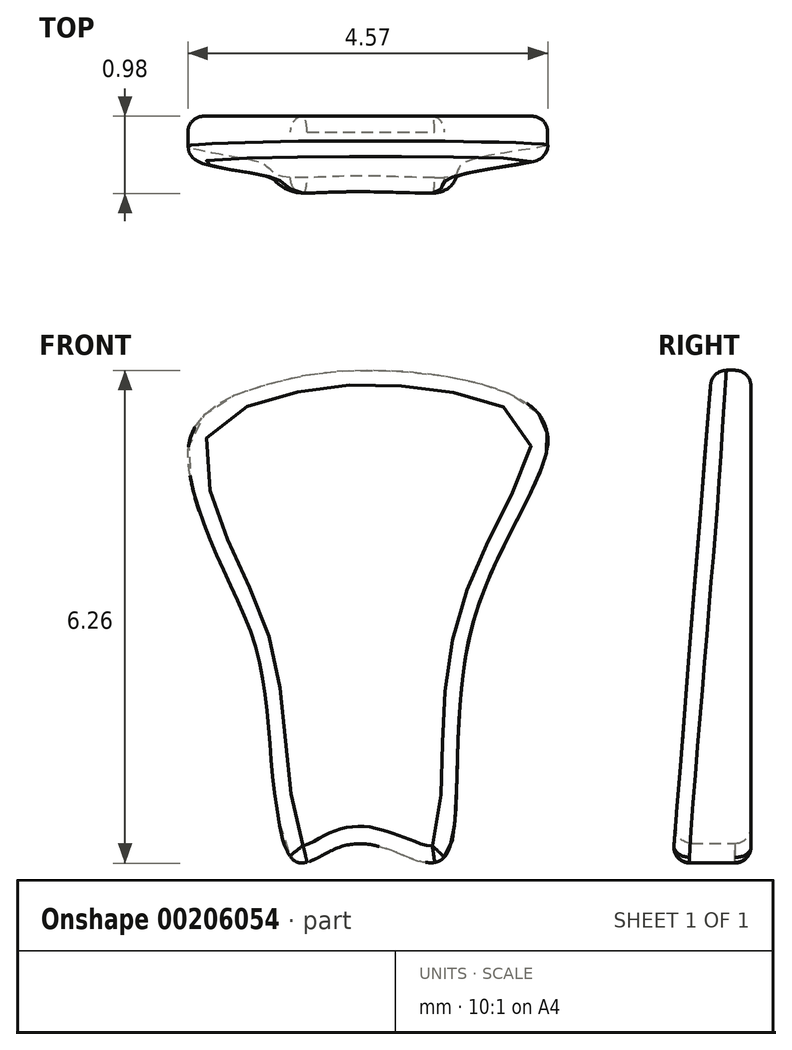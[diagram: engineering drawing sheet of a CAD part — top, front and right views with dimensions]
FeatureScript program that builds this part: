
annotation { "Feature Type Name" : "Feature", "Feature Type Description" : "" }
export const myFeature = defineFeature(function(context is Context, id is Id, definition is map)
    precondition{}
    {
        {
            var Q0;
            Q0=qCreatedBy(makeId("Front.planeOp"),FACE);
            var sketch = newSketch(context, id + "F0", { "sketchPlane" : qUnion([Q0])});
            skPoint(sketch, "E0", {"position": v(-0.76, -3.9) * mm});
            skPoint(sketch, "E1", {"position": v(1.07, -3.89) * mm});
            skPoint(sketch, "E2", {"position": v(1.47, -0.96) * mm});
            skPoint(sketch, "E3", {"position": v(2.4, 1.67) * mm});
            skPoint(sketch, "E4", {"position": v(0.49, 2.33) * mm});
            skPoint(sketch, "E5", {"position": v(-1.15, 2.16) * mm});
            skPoint(sketch, "E6", {"position": v(-2.1, 1.49) * mm});
            skPoint(sketch, "E7", {"position": v(-1.57, -0.44) * mm});
            skPoint(sketch, "E8", {"position": v(-1.15, -1.8) * mm});
            skPoint(sketch, "E9", {"position": v(0, -3.67) * mm});
            skFitSpline(sketch, "E10", {"points": [v(-2.1, 1.49) * mm, v(-1.15, 2.16) * mm, v(0.49, 2.33) * mm, v(2.4, 1.67) * mm, v(1.47, -0.96) * mm, v(1.07, -3.89) * mm, v(0, -3.67) * mm, v(-0.76, -3.9) * mm, v(-1.15, -1.8) * mm, v(-1.57, -0.44) * mm, v(-2.1, 1.49) * mm]});
            skSolve(sketch);
        }
        {
            var Q0;
            Q0 = qSketchRegion(id + "F0", true);
            extrude(context, id + "F1", {"entities" : qUnion([Q0]), "depth" : 1 * mm});
        }
        {
            var Q0;
            Q0=qCreatedBy(makeId("Right.planeOp"),FACE);
            var sketch = newSketch(context, id + "F2", { "sketchPlane" : qUnion([Q0])});
            skLineSegment(sketch, "E11", {"start": v(-0.44, 3.04) * mm, "end": v(-1.07, -4.82) * mm});
            skLineSegment(sketch, "E12", {"start": v(-1.07, -4.82) * mm, "end": v(-1.07, 2.98) * mm});
            skLineSegment(sketch, "E13", {"start": v(-1.07, 2.98) * mm, "end": v(-0.44, 3.04) * mm});
            skSolve(sketch);
        }
        {
            var Q0;
            Q0 = qSketchRegion(id + "F2", true);
            extrude(context, id + "F3", {"entities" : qUnion([Q0]), "operationType" : NewBodyOperationType.REMOVE, "oppositeDirection" : true, "depth" : 25 * mm, "hasSecondDirection" : true, "secondDirectionOppositeDirection" : false, "secondDirectionDepth" : 25 * mm});
        }
        {
            var Q0;
            Q0=makeQuery(id+"F3.boolean.opBoolean","COPY",FACE,{"derivedFrom":makeQuery(id+"F3.opExtrude","SWEPT_FACE",FACE,{"disambiguationData":[OSD([sQuery(id+"F2.wireOp",EDGE,"E11")])]})});
            fillet(context, id + "F4", {"entities" : qUnion([Q0]), "radius" : 0.2 * mm, "tangentPropagation" : true, "allowEdgeOverflow" : false});
        }
        {
            var Q0;
            Q0=makeQuery(id+"F1.opExtrude","CAP_FACE",FACE,{"disambiguationData":[OSD([sQuery(id+"F0.wireOp",EDGE,"E10")])],"isStart":true});
            fillet(context, id + "F5", {"entities" : qUnion([Q0]), "radius" : 0.2 * mm, "tangentPropagation" : true, "allowEdgeOverflow" : false});
        }
    });
